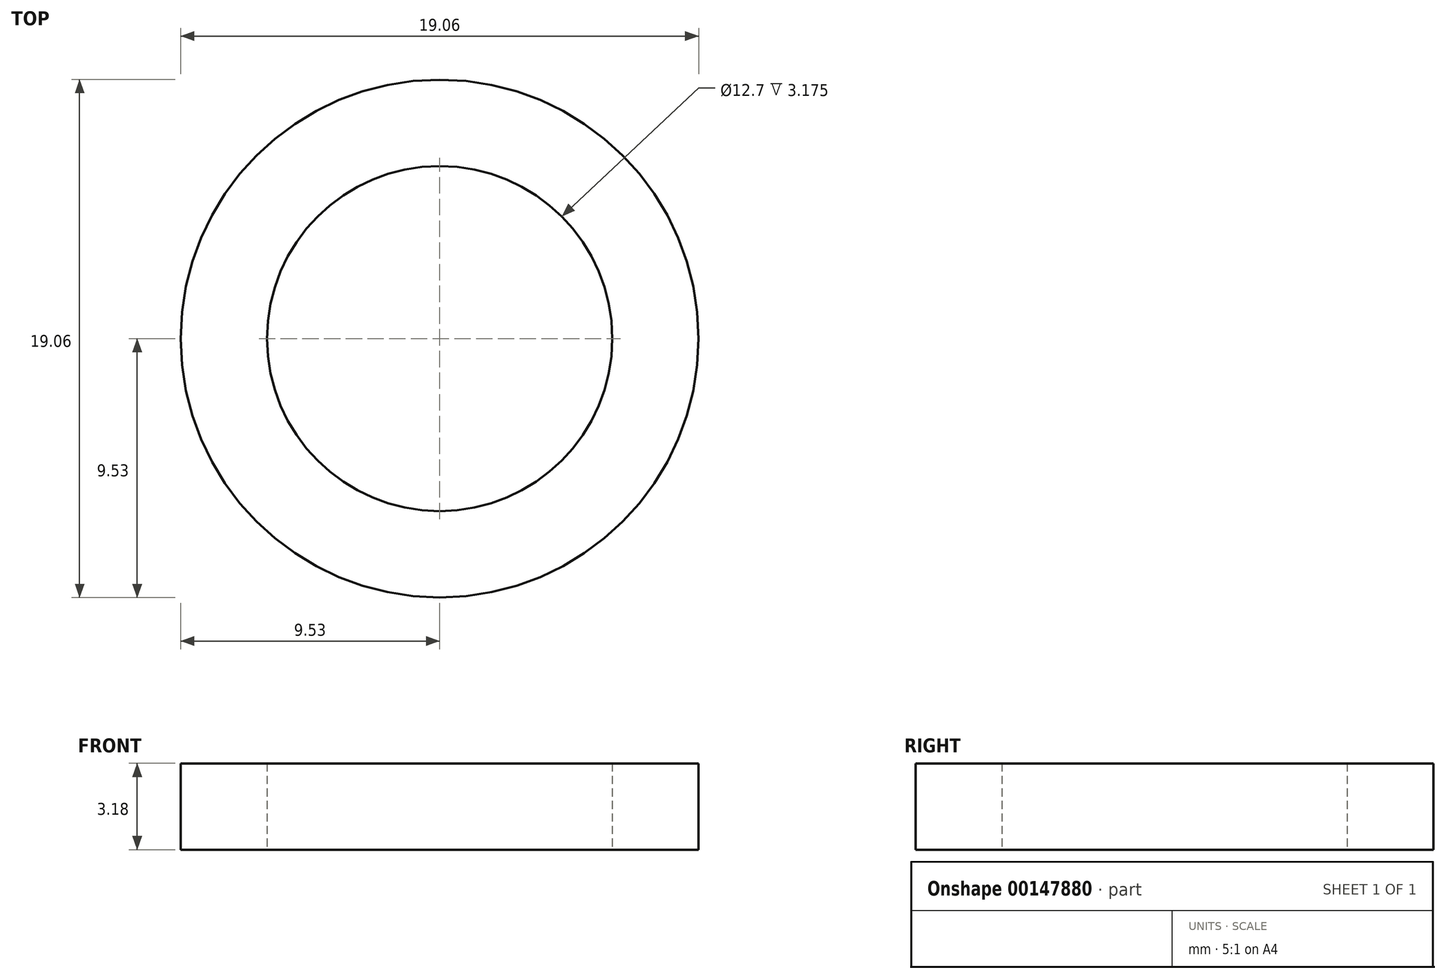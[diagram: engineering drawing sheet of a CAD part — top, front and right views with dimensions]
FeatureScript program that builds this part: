
annotation { "Feature Type Name" : "Feature", "Feature Type Description" : "" }
export const myFeature = defineFeature(function(context is Context, id is Id, definition is map)
    precondition{}
    {
        {
            var Q0;
            Q0=qCreatedBy(makeId("Top.planeOp"),FACE);
            var sketch = newSketch(context, id + "F0", { "sketchPlane" : qUnion([Q0])});
            skCircle(sketch, "E0", {"center": v(0, 0) * mm, "radius": 6.35 * mm});
            skCircle(sketch, "E1", {"center": v(0, 0) * mm, "radius": 9.53 * mm});
            skSolve(sketch);
        }
        {
            var Q0;
            Q0=qSketchRegion(id+"F0",true);
            extrude(context, id + "F1", {"entities" : qUnion([Q0]), "depth" : 3.17 * mm});
        }
    });
